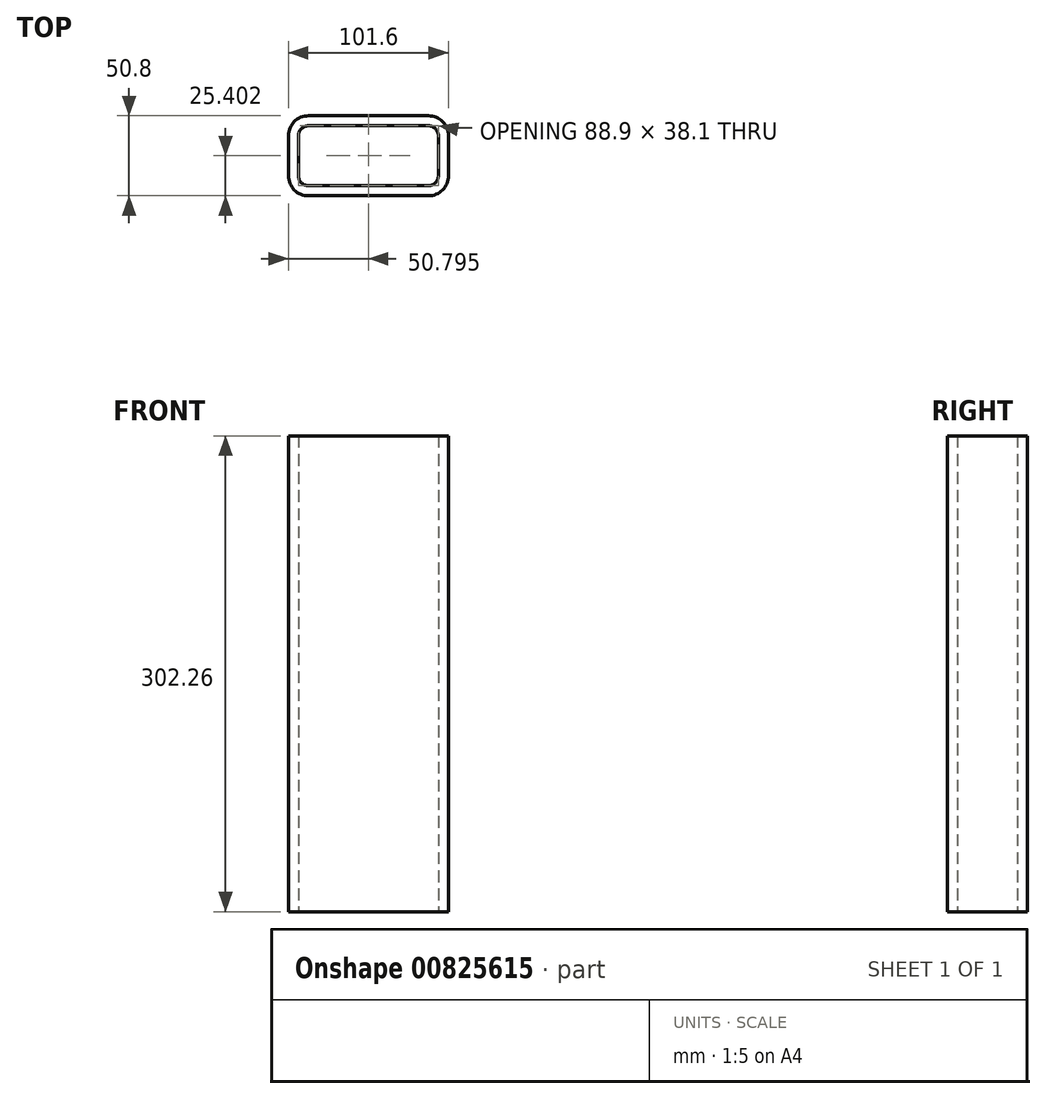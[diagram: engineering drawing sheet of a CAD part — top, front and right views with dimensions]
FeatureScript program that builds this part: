
annotation { "Feature Type Name" : "Feature", "Feature Type Description" : "" }
export const myFeature = defineFeature(function(context is Context, id is Id, definition is map)
    precondition{}
    {
        {
            var Q0;
            Q0=qCreatedBy(makeId("Top.planeOp"),FACE);
            var sketch = newSketch(context, id + "F0", { "sketchPlane" : qUnion([Q0])});
            skLineSegment(sketch, "E0.0", {"start": v(162.88, 54.95) * mm, "end": v(239.08, 54.95) * mm});
            skLineSegment(sketch, "E1.0", {"start": v(162.88, 16.85) * mm, "end": v(239.08, 16.85) * mm});
            skLineSegment(sketch, "E2.0", {"start": v(156.53, 23.2) * mm, "end": v(156.53, 48.6) * mm});
            skLineSegment(sketch, "E3.0", {"start": v(245.43, 23.2) * mm, "end": v(245.43, 48.6) * mm});
            skArc(sketch, "E4.filletArc", {"start": v(162.88, 54.95) * mm, "mid": v(158.39, 53.1) * mm, "end": v(156.53, 48.6) * mm});
            skArc(sketch, "E5.filletArc", {"start": v(156.53, 23.2) * mm, "mid": v(158.39, 18.71) * mm, "end": v(162.88, 16.85) * mm});
            skArc(sketch, "E6.filletArc", {"start": v(245.43, 48.6) * mm, "mid": v(243.57, 53.1) * mm, "end": v(239.08, 54.95) * mm});
            skArc(sketch, "E7.filletArc", {"start": v(239.08, 16.85) * mm, "mid": v(243.57, 18.71) * mm, "end": v(245.43, 23.2) * mm});
            skLineSegment(sketch, "E8.0", {"start": v(251.78, 23.2) * mm, "end": v(251.78, 48.6) * mm});
            skArc(sketch, "E8.1", {"start": v(239.08, 10.5) * mm, "mid": v(248.06, 14.22) * mm, "end": v(251.78, 23.2) * mm});
            skArc(sketch, "E8.2", {"start": v(251.78, 48.6) * mm, "mid": v(248.06, 57.58) * mm, "end": v(239.08, 61.3) * mm});
            skLineSegment(sketch, "E8.3", {"start": v(162.88, 10.5) * mm, "end": v(239.08, 10.5) * mm});
            skLineSegment(sketch, "E8.4", {"start": v(162.88, 61.3) * mm, "end": v(239.08, 61.3) * mm});
            skArc(sketch, "E8.5", {"start": v(162.88, 61.3) * mm, "mid": v(153.9, 57.58) * mm, "end": v(150.18, 48.6) * mm});
            skLineSegment(sketch, "E8.6", {"start": v(150.18, 23.2) * mm, "end": v(150.18, 48.6) * mm});
            skArc(sketch, "E8.7", {"start": v(150.18, 23.2) * mm, "mid": v(153.9, 14.22) * mm, "end": v(162.88, 10.5) * mm});
            skLineSegment(sketch, "E9", {"start": v(0, 0) * mm, "end": v(-256.68, 0) * mm});
            skLineSegment(sketch, "E10.0", {"start": v(0, 50.8) * mm, "end": v(-256.68, 50.8) * mm});
            skLineSegment(sketch, "E11.0", {"start": v(0, 1193.8) * mm, "end": v(-256.68, 1193.8) * mm});
            skLineSegment(sketch, "E12.0", {"start": v(0, 1244.6) * mm, "end": v(-256.68, 1244.6) * mm});
            skLineSegment(sketch, "E13.0", {"start": v(0, 2254.25) * mm, "end": v(-256.68, 2254.25) * mm});
            skSolve(sketch);
        }
        {
            var Q0;
            Q0=makeQuery(id+"F0.imprint","IMPRINT",FACE,{"disambiguationData":[TD([[makeQuery(id+"F0.imprint","IMPRINT",EDGE,{"derivedFrom":sQuery(id+"F0.wireOp",EDGE,"E0.0")}),1.0]])]});
            extrude(context, id + "F1", {"entities" : qUnion([Q0]), "depth" : 302.26 * mm, "offsetDistance" : 25.4 * mm});
        }
    });
